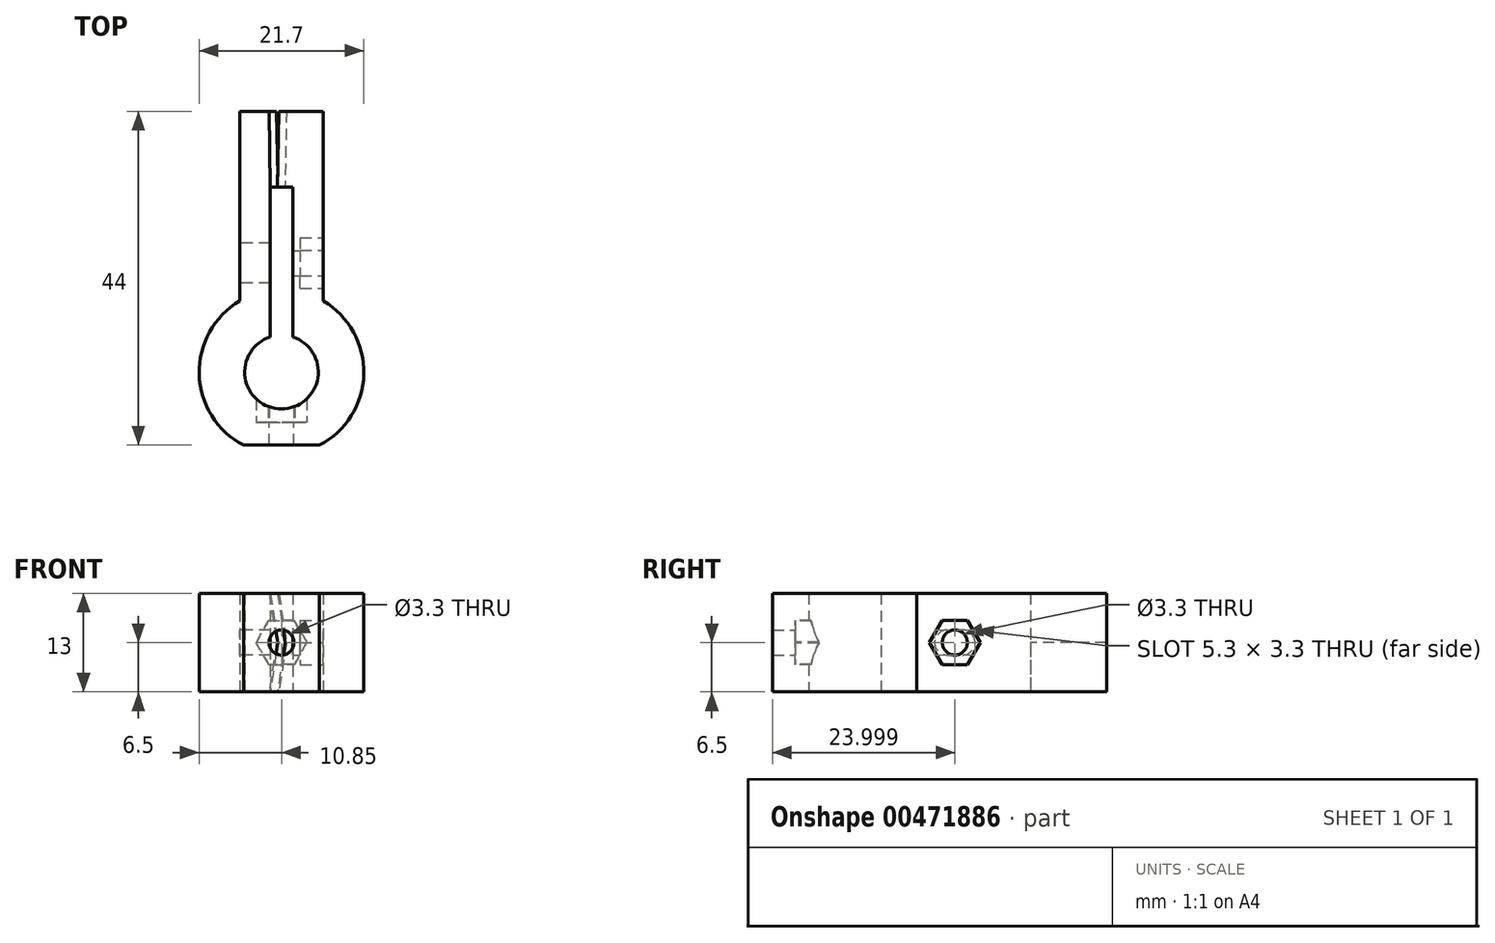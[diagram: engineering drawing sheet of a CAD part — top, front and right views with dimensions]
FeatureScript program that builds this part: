
annotation { "Feature Type Name" : "Feature", "Feature Type Description" : "" }
export const myFeature = defineFeature(function(context is Context, id is Id, definition is map)
    precondition{}
    {
        {
            var Q0;
            Q0=qCreatedBy(makeId("Top.planeOp"),FACE);
            var sketch = newSketch(context, id + "F0", { "sketchPlane" : qUnion([Q0])});
            skArc(sketch, "E0", {"start": v(5, 0) * mm, "mid": v(10.85, 9.36) * mm, "end": v(5.48, 19) * mm});
            skLineSegment(sketch, "E1", {"start": v(5.48, 19) * mm, "end": v(5.48, 44) * mm});
            skLineSegment(sketch, "E2", {"start": v(5.48, 44) * mm, "end": v(0.65, 44) * mm});
            skLineSegment(sketch, "E3", {"start": v(0.65, 44) * mm, "end": v(0.48, 34) * mm});
            skLineSegment(sketch, "E4", {"start": v(0.48, 34) * mm, "end": v(1.48, 34) * mm});
            skLineSegment(sketch, "E5", {"start": v(1.48, 34) * mm, "end": v(1.48, 14.25) * mm});
            skLineSegment(sketch, "E6", {"start": v(0, 4.78) * mm, "end": v(0, 0) * mm});
            skArc(sketch, "E7", {"start": v(0, 4.78) * mm, "mid": v(4.8, 8.88) * mm, "end": v(1.48, 14.25) * mm});
            skLineSegment(sketch, "E8", {"start": v(0, 9.63) * mm, "end": v(0.08, 14.26) * mm, "construction": true});
            skLineSegment(sketch, "E9", {"start": v(0, 0) * mm, "end": v(5, 0) * mm});
            skSolve(sketch);
        }
        {
            var Q0;
            Q0 = qSketchRegion(id + "F0", true);
            extrude(context, id + "F1", {"entities" : qUnion([Q0]), "depth" : 13 * mm});
        }
        {
            var Q0;
            Q0=makeQuery(id+"F1.opExtrude","SWEPT_BODY",BODY,{"disambiguationData":[OSD([sQuery(id+"F0.wireOp",EDGE,"jemivE3e-jwHB-FYLw-It3T-QXnUrjt0YGzj"),sQuery(id+"F0.wireOp",EDGE,"bCWJ0XCk-YWtU-moQV-jBBy-W2zocU8WDkey"),sQuery(id+"F0.wireOp",EDGE,"E0"),sQuery(id+"F0.wireOp",EDGE,"E1"),sQuery(id+"F0.wireOp",EDGE,"E2"),sQuery(id+"F0.wireOp",EDGE,"E3"),sQuery(id+"F0.wireOp",EDGE,"E4"),sQuery(id+"F0.wireOp",EDGE,"E5"),sQuery(id+"F0.wireOp",EDGE,"IBKc2iPw-RDQO-q08Q-gl9g-pQ8c8ZBI7A2v"),sQuery(id+"F0.wireOp",EDGE,"FMwJBpQ0-P6oV-9bJx-Ru70-hiZCuK0YFgAS"),sQuery(id+"F0.wireOp",EDGE,"E6")])]});
            var Q1;
            Q1=qCreatedBy(makeId("Right.planeOp"),FACE);
            mirror(context, id + "F2", {"operationType" : NewBodyOperationType.ADD, "entities" : qUnion([Q0]), "mirrorPlane" : qUnion([Q1])});
        }
        {
            var Q0;
            Q0=makeQuery(id+"F1.opExtrude","SWEPT_FACE",FACE,{"disambiguationData":[OSD([sQuery(id+"F0.wireOp",EDGE,"E1")])]});
            var sketch = newSketch(context, id + "F3", { "sketchPlane" : qUnion([Q0])});
            skCircle(sketch, "E10.cCircle", {"center": v(24, 6.5) * mm, "radius": 2.9 * mm, "construction": true});
            skLineSegment(sketch, "E10.0", {"start": v(25.67, 3.6) * mm, "end": v(22.32, 3.6) * mm});
            skLineSegment(sketch, "E10.1", {"start": v(22.32, 3.6) * mm, "end": v(20.65, 6.5) * mm});
            skLineSegment(sketch, "E10.2", {"start": v(20.65, 6.5) * mm, "end": v(22.32, 9.4) * mm});
            skLineSegment(sketch, "E10.3", {"start": v(22.32, 9.4) * mm, "end": v(25.67, 9.4) * mm});
            skLineSegment(sketch, "E10.4", {"start": v(25.67, 9.4) * mm, "end": v(27.35, 6.5) * mm});
            skLineSegment(sketch, "E10.5", {"start": v(27.35, 6.5) * mm, "end": v(25.67, 3.6) * mm});
            skPoint(sketch, "E10.0.midPoint", {"position": v(24, 3.6) * mm});
            skLineSegment(sketch, "E11", {"start": v(24, 13) * mm, "end": v(24, 0) * mm, "construction": true});
            skSolve(sketch);
        }
        {
            var Q0;
            Q0=qSketchRegion(id+"F3",true);
            extrude(context, id + "F4", {"entities" : qUnion([Q0]), "operationType" : NewBodyOperationType.REMOVE, "oppositeDirection" : true, "depth" : 3 * mm});
        }
        {
            var Q0;
            Q0=makeQuery(id+"F4.boolean.opBoolean","COPY",FACE,{"derivedFrom":makeQuery(id+"F4.opExtrude","CAP_FACE",FACE,{"disambiguationData":[OSD([sQuery(id+"F3.wireOp",EDGE,"E10.0"),sQuery(id+"F3.wireOp",EDGE,"E10.1"),sQuery(id+"F3.wireOp",EDGE,"E10.2"),sQuery(id+"F3.wireOp",EDGE,"E10.3"),sQuery(id+"F3.wireOp",EDGE,"E10.4"),sQuery(id+"F3.wireOp",EDGE,"E10.5")])],"isStart":false})});
            var sketch = newSketch(context, id + "F5", { "sketchPlane" : qUnion([Q0])});
            skCircle(sketch, "E12", {"center": v(24, 6.5) * mm, "radius": 1.65 * mm});
            skLineSegment(sketch, "E13", {"start": v(22.32, 9.4) * mm, "end": v(25.67, 3.6) * mm, "construction": true});
            skSolve(sketch);
        }
        {
            var Q0;
            Q0=makeQuery(id+"F5.imprint","IMPRINT",FACE,{"disambiguationData":[TD([[makeQuery(id+"F5.imprint","IMPRINT",EDGE,{"derivedFrom":sQuery(id+"F5.wireOp",EDGE,"E12")}),1.0]])]});
            var Q1;
            Q1=sQuery(id+"F5.wireOp",EDGE,"E12");
            extrude(context, id + "F6", {"entities" : qUnion([Q0]), "operationType" : NewBodyOperationType.REMOVE, "surfaceEntities" : qUnion([Q1]), "endBound" : BoundingType.UP_TO_NEXT, "oppositeDirection" : true, "depth" : 25 * mm});
        }
        {
            var Q0;
            Q0=makeQuery(id+"F2.opPattern","COPY",FACE,{"derivedFrom":makeQuery(id+"F1.opExtrude","SWEPT_FACE",FACE,{"disambiguationData":[OSD([sQuery(id+"F0.wireOp",EDGE,"E1")])]}),"instanceName":"1"});
            var sketch = newSketch(context, id + "F7", { "sketchPlane" : qUnion([Q0])});
            skLineSegment(sketch, "E14", {"start": v(-25, 6.5) * mm, "end": v(-23, 6.5) * mm, "construction": true});
            skArc(sketch, "E15", {"start": v(-23, 8.15) * mm, "mid": v(-21.35, 6.5) * mm, "end": v(-23, 4.85) * mm});
            skArc(sketch, "E16", {"start": v(-25, 8.15) * mm, "mid": v(-26.65, 6.5) * mm, "end": v(-25, 4.85) * mm});
            skLineSegment(sketch, "E17", {"start": v(-25, 8.15) * mm, "end": v(-23, 8.15) * mm});
            skLineSegment(sketch, "E18", {"start": v(-23, 4.85) * mm, "end": v(-25, 4.85) * mm});
            skLineSegment(sketch, "E19", {"start": v(-25, 13) * mm, "end": v(-25, 0) * mm, "construction": true});
            skSolve(sketch);
        }
        {
            var Q0;
            Q0=qSketchRegion(id+"F7",true);
            extrude(context, id + "F8", {"entities" : qUnion([Q0]), "operationType" : NewBodyOperationType.REMOVE, "endBound" : BoundingType.UP_TO_NEXT, "oppositeDirection" : true, "depth" : 25 * mm});
        }
        {
            var Q0;
            Q0=qCreatedBy(makeId("Front.planeOp"),FACE);
            cPlane(context, id + "F9", {"entities" : qUnion([Q0]), "cplaneType" : CPlaneType.OFFSET, "offset" : 5 * mm, "oppositeDirection" : true, "width" : 150 * mm, "height" : 150 * mm});
        }
        {
            var Q0;
            Q0=qCreatedBy(id+"F9.planeOp",FACE);
            var sketch = newSketch(context, id + "F10", { "sketchPlane" : qUnion([Q0])});
            skCircle(sketch, "E20.cCircle", {"center": v(0, 6.5) * mm, "radius": 2.9 * mm, "construction": true});
            skLineSegment(sketch, "E20.0", {"start": v(3.35, 6.57) * mm, "end": v(1.74, 3.64) * mm});
            skLineSegment(sketch, "E20.1", {"start": v(1.74, 3.64) * mm, "end": v(-1.61, 3.56) * mm});
            skLineSegment(sketch, "E20.2", {"start": v(-1.61, 3.56) * mm, "end": v(-3.35, 6.43) * mm});
            skLineSegment(sketch, "E20.3", {"start": v(-3.35, 6.43) * mm, "end": v(-1.74, 9.36) * mm});
            skLineSegment(sketch, "E20.4", {"start": v(-1.74, 9.36) * mm, "end": v(1.61, 9.44) * mm});
            skLineSegment(sketch, "E20.5", {"start": v(1.61, 9.44) * mm, "end": v(3.35, 6.57) * mm});
            skPoint(sketch, "E20.0.midPoint", {"position": v(2.54, 5.1) * mm});
            skLineSegment(sketch, "E21", {"start": v(0, 13) * mm, "end": v(0, 0) * mm, "construction": true});
            skSolve(sketch);
        }
        {
            var Q0;
            Q0=qSketchRegion(id+"F10",true);
            extrude(context, id + "F11", {"entities" : qUnion([Q0]), "operationType" : NewBodyOperationType.REMOVE, "oppositeDirection" : true, "depth" : 3 * mm, "hasSecondDirection" : true, "secondDirectionOppositeDirection" : false, "secondDirectionDepth" : 2 * mm});
        }
        {
            var Q0;
            Q0=makeQuery(id+"F11.boolean.opBoolean","COPY",FACE,{"derivedFrom":makeQuery(id+"F11.opExtrude","CAP_FACE",FACE,{"disambiguationData":[OSD([sQuery(id+"F10.wireOp",EDGE,"E20.0"),sQuery(id+"F10.wireOp",EDGE,"E20.1"),sQuery(id+"F10.wireOp",EDGE,"E20.2"),sQuery(id+"F10.wireOp",EDGE,"E20.3"),sQuery(id+"F10.wireOp",EDGE,"E20.4"),sQuery(id+"F10.wireOp",EDGE,"E20.5")])],"isStart":true})});
            var sketch = newSketch(context, id + "F12", { "sketchPlane" : qUnion([Q0])});
            skLineSegment(sketch, "E22", {"start": v(-1.61, 9.44) * mm, "end": v(1.61, 3.56) * mm, "construction": true});
            skCircle(sketch, "E23", {"center": v(0, 6.5) * mm, "radius": 1.65 * mm});
            skSolve(sketch);
        }
        {
            var Q0;
            Q0=qSketchRegion(id+"F12",true);
            extrude(context, id + "F13", {"entities" : qUnion([Q0]), "operationType" : NewBodyOperationType.REMOVE, "endBound" : BoundingType.UP_TO_NEXT, "oppositeDirection" : true, "depth" : 25 * mm});
        }
        {
            var Q0;
            Q0=makeQuery(id+"F2.opPattern","COPY",FACE,{"derivedFrom":makeQuery(id+"F1.opExtrude","SWEPT_FACE",FACE,{"disambiguationData":[OSD([sQuery(id+"F0.wireOp",EDGE,"E2")])]}),"instanceName":"1"});
            var sketch = newSketch(context, id + "F14", { "sketchPlane" : qUnion([Q0])});
            skLineSegment(sketch, "E24", {"start": v(1.65, 13) * mm, "end": v(0.65, 6.5) * mm});
            skLineSegment(sketch, "E25", {"start": v(0.65, 6.5) * mm, "end": v(1.65, 0) * mm});
            skLineSegment(sketch, "E26", {"start": v(1.65, 13) * mm, "end": v(0.45, 13) * mm});
            skLineSegment(sketch, "E27", {"start": v(0.45, 13) * mm, "end": v(0.45, 0) * mm});
            skLineSegment(sketch, "E28", {"start": v(0.45, 0) * mm, "end": v(1.65, 0) * mm});
            skSolve(sketch);
        }
        {
            var Q0;
            Q0=qSketchRegion(id+"F14",true);
            var Q1;
            Q1=makeQuery(id+"F2.opPattern","COPY",EDGE,{"derivedFrom":makeQuery(id+"F1.opExtrude","CAP_EDGE",EDGE,{"disambiguationData":[OSD([sQuery(id+"F0.wireOp",EDGE,"E3")])],"isStart":false}),"instanceName":"1"});
            sweep(context, id + "F15", {"operationType" : NewBodyOperationType.REMOVE, "profiles" : qUnion([Q0]), "path" : qUnion([Q1])});
        }
        {
            var Q0;
            Q0=makeQuery(id+"F1.opExtrude","SWEPT_FACE",FACE,{"disambiguationData":[OSD([sQuery(id+"F0.wireOp",EDGE,"E2")])]});
            var sketch = newSketch(context, id + "F16", { "sketchPlane" : qUnion([Q0])});
            skLineSegment(sketch, "E29", {"start": v(0.35, 13) * mm, "end": v(-0.65, 6.5) * mm});
            skLineSegment(sketch, "E30", {"start": v(-0.65, 6.5) * mm, "end": v(0.35, 0) * mm});
            skLineSegment(sketch, "E31", {"start": v(-1.31, 13) * mm, "end": v(0.35, 13) * mm});
            skLineSegment(sketch, "E32", {"start": v(-1.31, 13) * mm, "end": v(-1.31, 0) * mm});
            skLineSegment(sketch, "E33", {"start": v(-1.31, 0) * mm, "end": v(0.35, 0) * mm});
            skLineSegment(sketch, "E34", {"start": v(-1.31, 6.5) * mm, "end": v(-0.65, 6.5) * mm, "construction": true});
            skSolve(sketch);
        }
        {
            var Q0;
            Q0=qSketchRegion(id+"F16",true);
            var Q1;
            Q1=makeQuery(id+"F1.opExtrude","CAP_EDGE",EDGE,{"disambiguationData":[OSD([sQuery(id+"F0.wireOp",EDGE,"E3")])],"isStart":false});
            sweep(context, id + "F17", {"operationType" : NewBodyOperationType.ADD, "profiles" : qUnion([Q0]), "path" : qUnion([Q1])});
        }
    });
